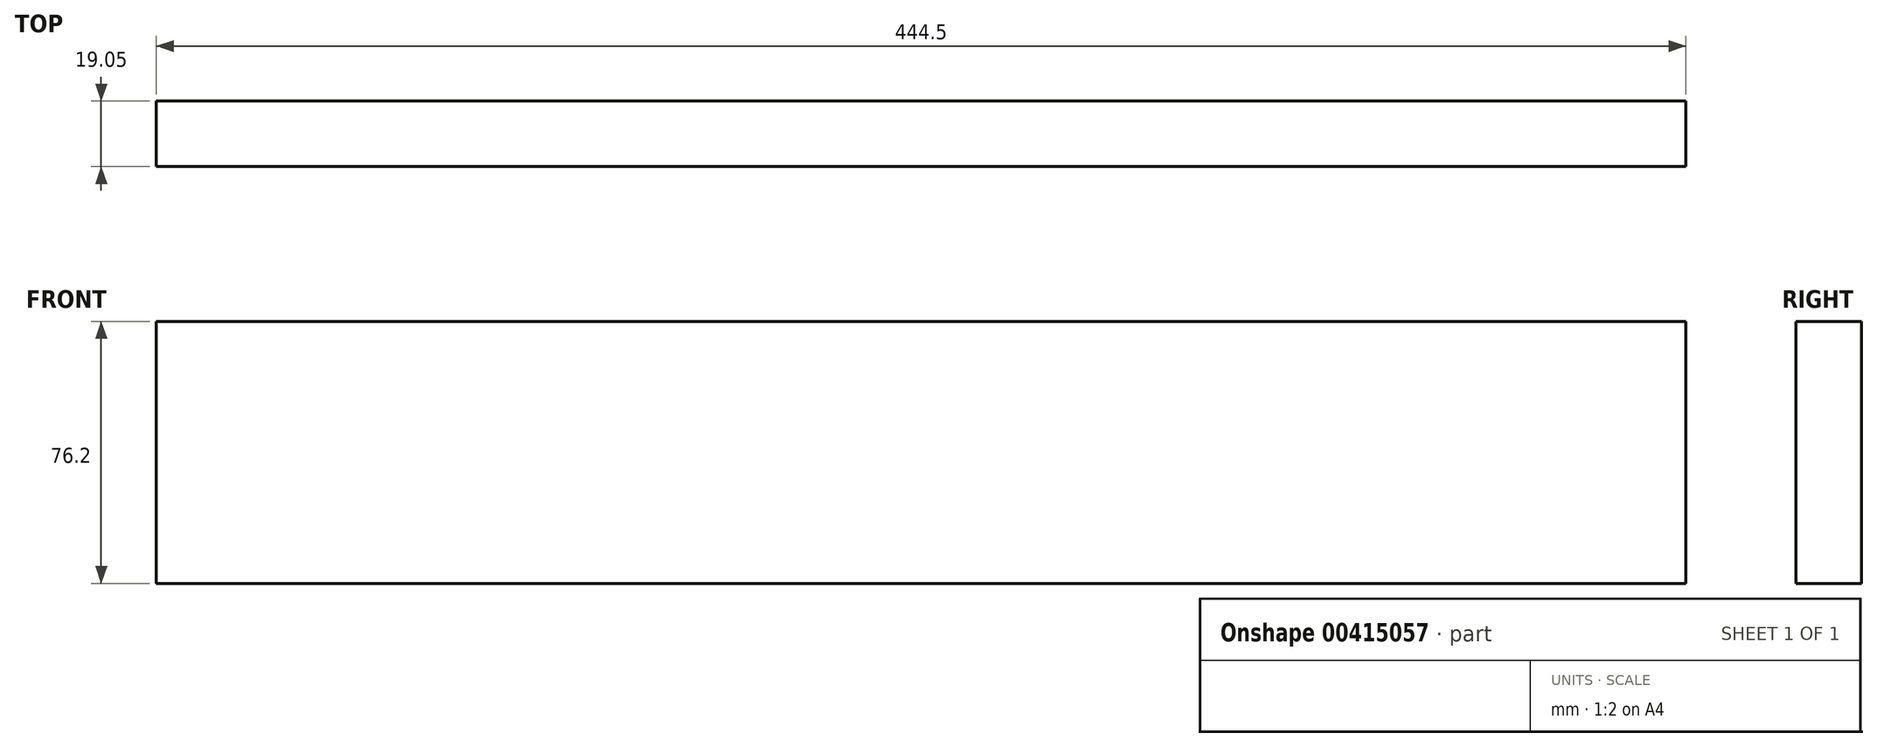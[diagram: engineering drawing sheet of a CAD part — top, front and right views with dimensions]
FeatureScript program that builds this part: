
annotation { "Feature Type Name" : "Feature", "Feature Type Description" : "" }
export const myFeature = defineFeature(function(context is Context, id is Id, definition is map)
    precondition{}
    {
        {
            var Q0;
            Q0=qCreatedBy(makeId("Front.planeOp"),FACE);
            var sketch = newSketch(context, id + "F0", { "sketchPlane" : qUnion([Q0])});
            skLineSegment(sketch, "E0.bottom", {"start": v(0, 0) * mm, "end": v(444.5, 0) * mm});
            skLineSegment(sketch, "E0.top", {"start": v(0, 76.2) * mm, "end": v(444.5, 76.2) * mm});
            skLineSegment(sketch, "E0.left", {"start": v(0, 0) * mm, "end": v(0, 76.2) * mm});
            skLineSegment(sketch, "E0.right", {"start": v(444.5, 0) * mm, "end": v(444.5, 76.2) * mm});
            skSolve(sketch);
        }
        {
            var Q0;
            Q0=makeQuery(id+"F0.imprint","IMPRINT",FACE,{"disambiguationData":[TD([[makeQuery(id+"F0.imprint","IMPRINT",EDGE,{"derivedFrom":sQuery(id+"F0.wireOp",EDGE,"E0.bottom")}),1.0]])]});
            extrude(context, id + "F1", {"entities" : qUnion([Q0]), "depth" : 19.05 * mm, "offsetDistance" : 25.4 * mm});
        }
    });
